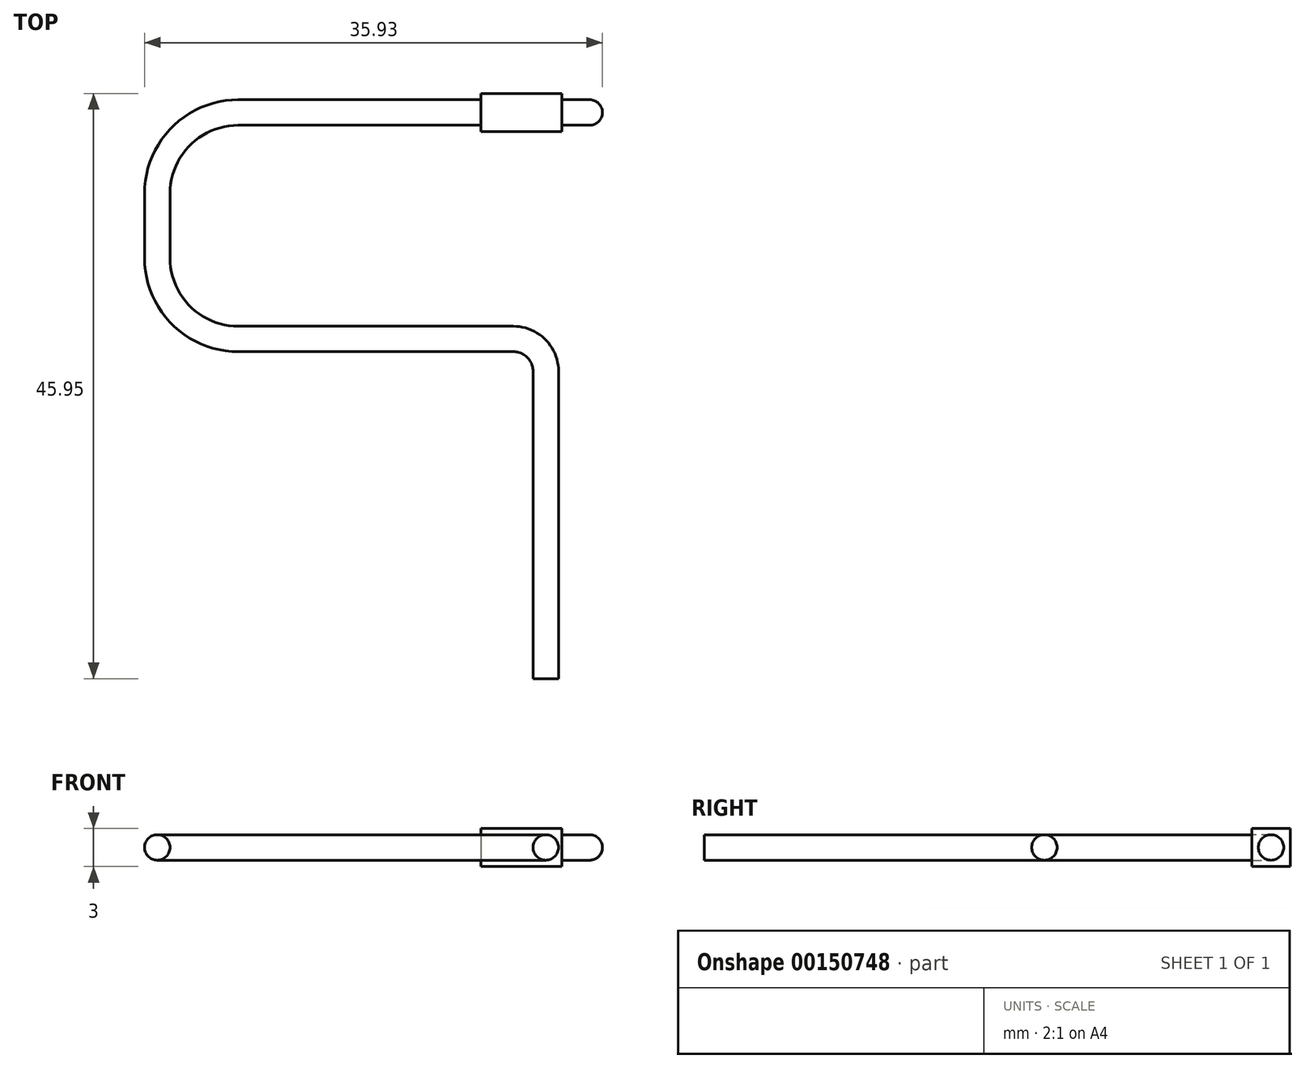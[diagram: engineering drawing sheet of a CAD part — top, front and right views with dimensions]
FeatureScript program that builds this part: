
annotation { "Feature Type Name" : "Feature", "Feature Type Description" : "" }
export const myFeature = defineFeature(function(context is Context, id is Id, definition is map)
    precondition{}
    {
        {
            var Q0;
            Q0=qCreatedBy(makeId("Right.planeOp"),FACE);
            var sketch = newSketch(context, id + "F0", { "sketchPlane" : qUnion([Q0])});
            skLineSegment(sketch, "E0.bottom", {"start": v(-1.5, 1.5) * mm, "end": v(1.5, 1.5) * mm});
            skLineSegment(sketch, "E0.top", {"start": v(-1.5, -1.5) * mm, "end": v(1.5, -1.5) * mm});
            skLineSegment(sketch, "E0.left", {"start": v(-1.5, 1.5) * mm, "end": v(-1.5, -1.5) * mm});
            skLineSegment(sketch, "E0.right", {"start": v(1.5, 1.5) * mm, "end": v(1.5, -1.5) * mm});
            skSolve(sketch);
        }
        {
            var Q0;
            Q0=makeQuery(id+"F0.imprint","IMPRINT",FACE,{"disambiguationData":[TD([[makeQuery(id+"F0.imprint","IMPRINT",EDGE,{"derivedFrom":sQuery(id+"F0.wireOp",EDGE,"E0.bottom")}),-1.0]])]});
            extrude(context, id + "F1", {"entities" : qUnion([Q0]), "depth" : 6.35 * mm});
        }
        {
            var Q0;
            Q0=makeQuery(id+"F1.opExtrude","CAP_FACE",FACE,{"disambiguationData":[OSD([sQuery(id+"F0.wireOp",EDGE,"E0.bottom"),sQuery(id+"F0.wireOp",EDGE,"E0.top"),sQuery(id+"F0.wireOp",EDGE,"E0.left"),sQuery(id+"F0.wireOp",EDGE,"E0.right")])],"isStart":false});
            var sketch = newSketch(context, id + "F2", { "sketchPlane" : qUnion([Q0])});
            skCircle(sketch, "E1", {"center": v(0, 0) * mm, "radius": 1 * mm});
            skSolve(sketch);
        }
        {
            var Q0;
            Q0=makeQuery(id+"F2.imprint","IMPRINT",FACE,{"disambiguationData":[TD([[makeQuery(id+"F2.imprint","IMPRINT",EDGE,{"derivedFrom":sQuery(id+"F2.wireOp",EDGE,"E1")}),1.0]])]});
            extrude(context, id + "F3", {"entities" : qUnion([Q0]), "operationType" : NewBodyOperationType.ADD, "depth" : 3.17 * mm});
        }
        {
            var Q0;
            Q0=makeQuery(id+"F3.opExtrude","CAP_EDGE",EDGE,{"disambiguationData":[OSD([sQuery(id+"F2.wireOp",EDGE,"E1")])],"isStart":false});
            fillet(context, id + "F4", {"entities" : qUnion([Q0]), "radius" : 1 * mm, "tangentPropagation" : true, "allowEdgeOverflow" : false});
        }
        {
            var Q0;
            Q0=makeQuery(id+"F1.opExtrude","CAP_FACE",FACE,{"disambiguationData":[OSD([sQuery(id+"F0.wireOp",EDGE,"E0.bottom"),sQuery(id+"F0.wireOp",EDGE,"E0.top"),sQuery(id+"F0.wireOp",EDGE,"E0.left"),sQuery(id+"F0.wireOp",EDGE,"E0.right")])],"isStart":true});
            var sketch = newSketch(context, id + "F5", { "sketchPlane" : qUnion([Q0])});
            skCircle(sketch, "E2", {"center": v(0, 0) * mm, "radius": 1 * mm});
            skSolve(sketch);
        }
        {
            var Q0;
            Q0=qCreatedBy(makeId("Top.planeOp"),FACE);
            var sketch = newSketch(context, id + "F6", { "sketchPlane" : qUnion([Q0])});
            skLineSegment(sketch, "E3", {"start": v(0, 0) * mm, "end": v(-19.05, 0) * mm});
            skArc(sketch, "E4", {"start": v(-19.05, 0) * mm, "mid": v(-23.54, -1.86) * mm, "end": v(-25.4, -6.35) * mm});
            skLineSegment(sketch, "E5", {"start": v(-25.4, -6.35) * mm, "end": v(-25.4, -11.43) * mm});
            skArc(sketch, "E6", {"start": v(-25.4, -11.43) * mm, "mid": v(-23.54, -15.92) * mm, "end": v(-19.05, -17.78) * mm});
            skLineSegment(sketch, "E7", {"start": v(-19.05, -17.78) * mm, "end": v(0, -17.78) * mm});
            skLineSegment(sketch, "E8", {"start": v(0, -17.78) * mm, "end": v(2.54, -17.78) * mm});
            skArc(sketch, "E9", {"start": v(5.08, -20.32) * mm, "mid": v(4.34, -18.52) * mm, "end": v(2.54, -17.78) * mm});
            skLineSegment(sketch, "E10", {"start": v(5.08, -20.32) * mm, "end": v(5.08, -44.45) * mm});
            skSolve(sketch);
        }
        {
            var Q0;
            {var subQ0=sQuery(id+"F5.wireOp",EDGE,"E2");var subQ1=makeQuery(id+"F1.opExtrude","CAP_EDGE",EDGE,{"disambiguationData":[OSD([sQuery(id+"F0.wireOp",EDGE,"E0.bottom")])],"isStart":true});var subQ2=makeQuery(id+"F5.imprint","INTERSECT",VERTEX,{"disambiguationData":[OD(0.0)],"derivedFrom":[subQ1,subQ0]});Q0=makeQuery(id+"F5.imprint","IMPRINT",FACE,{"disambiguationData":[TD([[makeQuery(id+"F5.imprint","IMPRINT",EDGE,{"disambiguationData":[TD([[subQ2,-1.0]])],"derivedFrom":subQ0}),1.0]])]});}
            var Q1;
            Q1=sQuery(id+"F6.wireOp",EDGE,"E3");
            var Q2;
            Q2=sQuery(id+"F6.wireOp",EDGE,"E4");
            var Q3;
            Q3=sQuery(id+"F6.wireOp",EDGE,"E5");
            var Q4;
            Q4=sQuery(id+"F6.wireOp",EDGE,"E6");
            var Q5;
            Q5=sQuery(id+"F6.wireOp",EDGE,"E7");
            var Q6;
            Q6=sQuery(id+"F6.wireOp",EDGE,"dlw1rrnv-c0I5-6YJv-e3HU-aNIzFhXRTsz4");
            var Q7;
            Q7=sQuery(id+"F6.wireOp",EDGE,"VVvcEyed-BSVS-5v4L-ydHg-89ACoWbgIjaX");
            var Q8;
            Q8=sQuery(id+"F6.wireOp",EDGE,"E8");
            var Q9;
            Q9=sQuery(id+"F6.wireOp",EDGE,"E9");
            var Q10;
            Q10=sQuery(id+"F6.wireOp",EDGE,"E10");
            sweep(context, id + "F7", {"operationType" : NewBodyOperationType.ADD, "profiles" : qUnion([Q0]), "path" : qUnion([Q1, Q2, Q3, Q4, Q5, Q6, Q7, Q8, Q9, Q10])});
        }
    });
